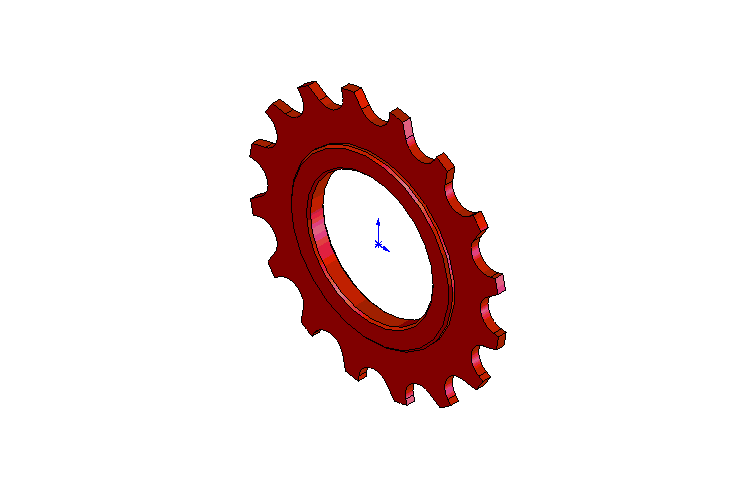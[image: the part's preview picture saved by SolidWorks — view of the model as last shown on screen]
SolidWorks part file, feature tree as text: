
SOLIDWORKS PART (.sldprt)
format: sldprt  version: not decoded by parser v0  size: 244,224 bytes
history: native  units: mm
features: sketch x4, plane x3, extrude x3, material x1, cut_extrude x1, pattern_circular x1, chamfer x1 (+10 scaffold rows collapsed)
feature tree (24):
  scaffold x10  (default folders/planes/origin — collapsed)
  material  "Matériau <non spécifié>"
  plane  "Plan de face"
  plane  "Plan de dessus"
  plane  "Plan de droite"
  sketch  "Esquisse1"  dims[D1=65.25mm]
  extrude  "Extrusion1"  Depth=2mm
  sketch  "Esquisse2"  dims[c1.D1=8.0mm c1.D3=4.0mm c2.D1=8.0mm c2.D3=4.0mm c2.D2=9.5mm c3.D3=4.0mm c3.D2=~2.039916mm c4.D2=35.0deg c4.D3=5.0mm]
  cut_extrude  "Enlèv. mat.-Extru.1"  [1 undecoded]
  pattern_circular  "Répétition circulaire1"  Count=16 Angle=22.5deg
  sketch  "Esquisse3"  dims[D1=42.0mm]
  extrude  "Extrusion2"  Depth=4.25mm
  sketch  "Esquisse4"  dims[D1=32.0mm]
  extrude  "Enlèv. mat.-Extru.2"  [1 undecoded]
  chamfer  "Chanfrein1"  Distance=0.5mm Angle=45deg
decode coverage: 8 of 10 modeling features carry decoded parameters
note: ~ marks probable driven/reference dimensions
note: 2 parameter values undecoded
note: suppression state not decoded; provenance and decode notes live in map.json
